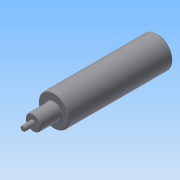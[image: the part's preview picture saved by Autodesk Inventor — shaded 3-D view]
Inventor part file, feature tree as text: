
AUTODESK INVENTOR PART (.ipt)
format: ipt  version: 2015 (Build 190159000, 159)  size: 109,568 bytes
history: native  units: mm
features: extrude x3, sketch x3, fillet x2
ambient origin geometry x8: Origin, YZ Plane, XZ Plane, XY Plane, X Axis, Y Axis, Z Axis, Center Point
bodies: Solid1 (feature_tree)
feature tree (8):
  extrude  "Extrusion1"  Depth=200.0mm TaperAngle=0.0deg
  extrude  "Extrusion2"  Depth=40.0mm TaperAngle=0.0deg
  extrude  "Extrusion3"  Depth=20.0mm TaperAngle=0.0deg
  fillet  "Fillet1"  Radius=2.0mm
  fillet  "Fillet2"  Radius=2.0mm
  sketch  "Sketch2"  dims[d0=60.0mm d1=200.0mm d2=0.0mm]
  sketch  "Sketch3"  dims[d3=30.0mm d4=40.0mm d5=0.0mm]
  sketch  "Sketch4"  dims[d6=10.0mm d7=20.0mm d8=0.0mm d9=2.0mm d10=2.0mm]
